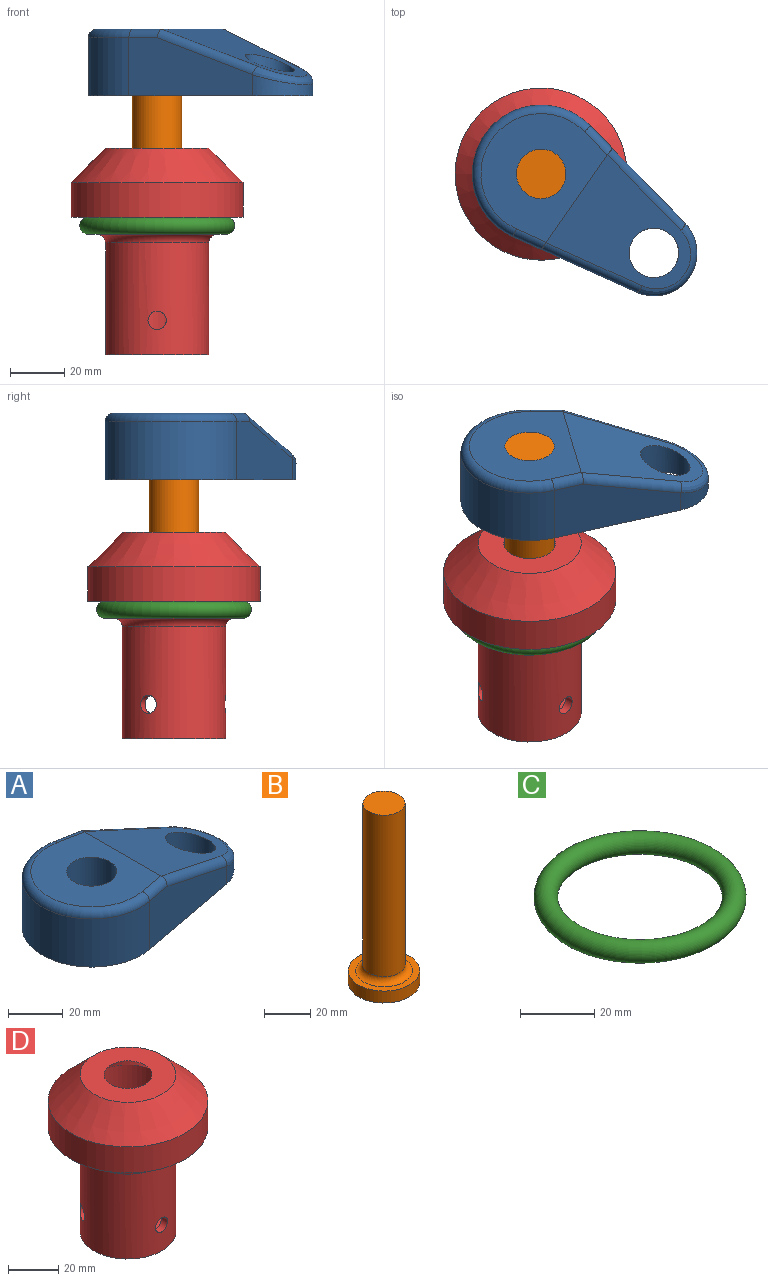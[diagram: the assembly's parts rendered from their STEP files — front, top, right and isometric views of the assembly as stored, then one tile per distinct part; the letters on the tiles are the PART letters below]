
ASSEMBLY  parts=4 mates=3
PART A: 15 faces, bbox 94.2x55x24.6 mm
  f0: plane 49.01x21.43mm, normal (0.19,0.98,0), area 807.2mm2, adj f2,f4,f5,f13,f14
  f1: plane 49.01x21.43mm, normal (0.19,-0.98,0), area 807.2mm2, adj f2,f4,f5,f9,f10
  f2: cylinder r=15.88mm len=31.19mm, axis (0,0,1), area 238.6mm2, adj f0,f1,f4,f12
  f3: cylinder r=9.13mm len=18.26mm, axis (0,0,1), area 691.4mm2, adj f4,f8
  f4: plane 92.08x50.8mm, normal (0,0,-1), area 3019.5mm2, adj f0,f1,f2,f3,f5,f7
  f5: cylinder r=25.4mm len=50.8mm, axis (0,0,1), area 1915.5mm2, adj f0,f1,f4,f11
  f6: plane 44.45x38.1mm, normal (0,0,1), area 1183.3mm2, adj f7,f8,f9,f11,f13
  f7: cylinder r=9.13mm len=24.61mm, axis (0,0,1), area 1411.3mm2, adj f4,f6
  f8: plane 48.71x39.6mm, normal (0.34,0,0.94), area 1243.5mm2, adj f3,f6,f9,f10,f12,f13,f14
  f9: cylinder r=3.17mm len=12.3mm, axis (0.98,0.19,0), area 58.4mm2, adj f1,f6,f8,f10,f11
  f10: cylinder r=3.17mm len=38.96mm, axis (-0.93,-0.18,0.33), area 197.2mm2, adj f1,f8,f9,f12
  f11: torus R=22.23mm, axis (0,0,1), area 425.5mm2, adj f5,f6,f9,f13
  f12: bspline ~31.19x12.89mm, area 173.4mm2, adj f2,f8,f10,f14
  f13: cylinder r=3.17mm len=12.3mm, axis (-0.98,0.19,0), area 58.4mm2, adj f0,f6,f8,f11,f14
  f14: cylinder r=3.17mm len=38.96mm, axis (0.93,-0.18,-0.33), area 197.2mm2, adj f0,f8,f12,f13
PART B: 6 faces, bbox 31x31x95.3 mm
  f0: plane 30.96x30.96mm, normal (0,0,-1), area 752.6mm2, adj f1
  f1: cylinder r=15.48mm len=30.96mm, axis (0,0,-1), area 617.5mm2, adj f0,f2
  f2: plane 30.96x30.96mm, normal (0,0,1), area 277.1mm2, adj f1,f5
  f3: cylinder r=9.13mm len=85.73mm, axis (0,0,-1), area 4916.6mm2, adj f4,f5
  f4: plane 18.26x18.26mm, normal (0,0,1), area 261.8mm2, adj f3
  f5: torus R=12.3mm, axis (0,0,-1), area 322.2mm2, adj f2,f3
PART C: 1 faces, bbox 61.9x61.9x6.4 mm
  f0: torus R=25.4mm, axis (0,0,1), area 3183.7mm2
PART D: 17 faces, bbox 63.5x63.5x76.2 mm
  f0: cylinder r=19.05mm len=41.28mm, axis (0,0,-1), area 4832.2mm2, adj f2,f10,f11,f12,f13
  f1: cylinder r=15.88mm len=63.5mm, axis (0,0,-1), area 6225.5mm2, adj f8,f9,f10,f11,f12
  f2: plane 38.1x38.1mm, normal (0,0,-1), area 855.1mm2, adj f0,f16
  f3: cylinder r=22.23mm len=44.45mm, axis (0,0,-1), area 443.4mm2, adj f13,f14
  f4: plane 63.5x63.5mm, normal (0,0,-1), area 1140.1mm2, adj f5,f14
  f5: cylinder r=31.75mm len=63.5mm, axis (0,0,-1), area 2533.5mm2, adj f4,f6
  f6: cone r=19.05mm half-angle=45deg, axis (0,0,-1), area 2866.4mm2, adj f5,f7
  f7: plane 38.1x38.1mm, normal (0,0,1), area 855.1mm2, adj f6,f8
  f8: cone r=9.53mm half-angle=45deg, axis (0,0,-1), area 716.6mm2, adj f1,f7
  f9: plane 31.75x31.75mm, normal (0,0,1), area 665.1mm2, adj f1,f15
  f10: cylinder r=3.38mm len=6.76mm, axis (0,1,0), area 68mm2, adj f0,f1
  f11: cylinder r=3.38mm len=7.62mm, axis (-0.87,-0.5,0), area 68mm2, adj f0,f1
  f12: cylinder r=3.38mm len=7.62mm, axis (0.87,-0.5,0), area 68mm2, adj f0,f1
  f13: torus R=22.23mm, axis (0,0,1), area 633.1mm2, adj f0,f3
  f14: torus R=25.4mm, axis (0,0,1), area 732.6mm2, adj f3,f4
  f15: cylinder r=6.35mm len=12.7mm, axis (0,0,-1), area 126.7mm2, adj f9,f16
  f16: cone r=6.35mm half-angle=45deg, axis (0,0,-1), area 223.9mm2, adj f2,f15
PLACE A rot(axis=(0,0,-1),35deg) t=(0,0,18.54)mm
PLACE B rot(axis=(0,0,-1),35deg) t=(0,0,18.54)mm
PLACE C t=(0,0,47.63)mm
PLACE D at identity fixed
MATE cylindrical B.f1 <-> D.f0  axis (0,0,-1) through (0,0,24.89)mm
MATE fastened C.f0 <-> D.f0  axis (0,0,1) through (0,0,47.63)mm
MATE fastened B.f1 <-> A.f5  axis (0,0,-1) through (0,0,120.14)mm
